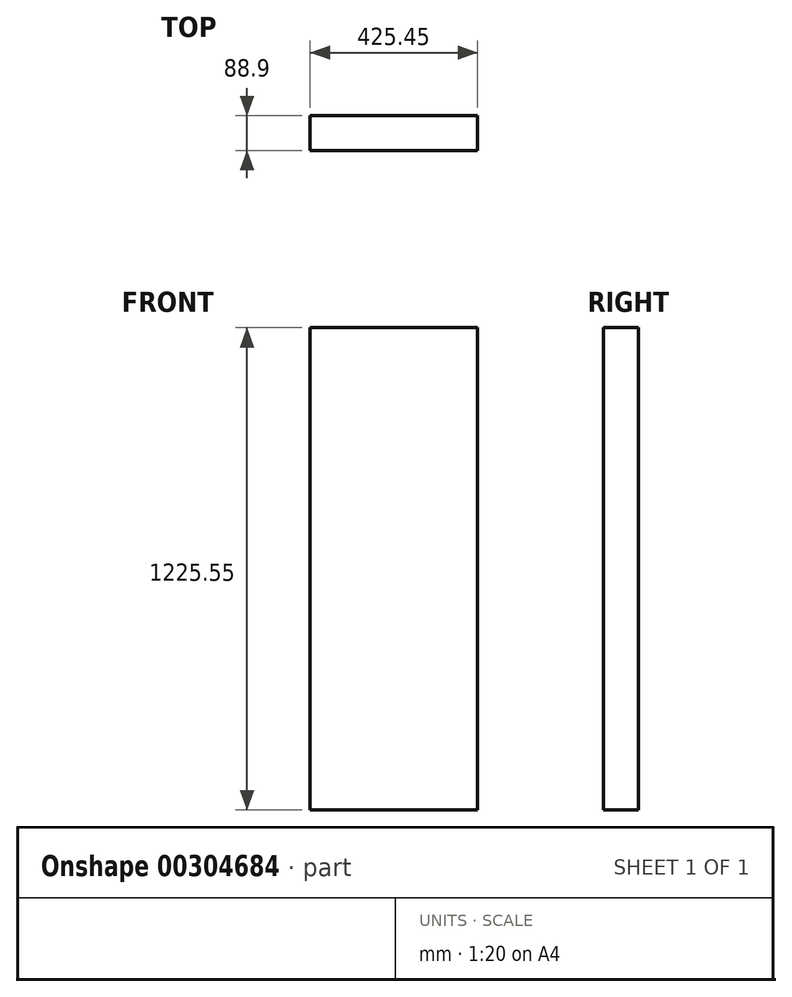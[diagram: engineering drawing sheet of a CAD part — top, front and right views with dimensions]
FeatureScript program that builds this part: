
annotation { "Feature Type Name" : "Feature", "Feature Type Description" : "" }
export const myFeature = defineFeature(function(context is Context, id is Id, definition is map)
    precondition{}
    {
        {
            var Q0;
            Q0=qCreatedBy(makeId("Front.planeOp"),FACE);
            var sketch = newSketch(context, id + "F0", { "sketchPlane" : qUnion([Q0])});
            skLineSegment(sketch, "E0.bottom", {"start": v(-210.24, 824.34) * mm, "end": v(215.21, 824.34) * mm});
            skLineSegment(sketch, "E0.top", {"start": v(-210.24, -401.21) * mm, "end": v(215.21, -401.21) * mm});
            skLineSegment(sketch, "E0.left", {"start": v(-210.24, 824.34) * mm, "end": v(-210.24, -401.21) * mm});
            skLineSegment(sketch, "E0.right", {"start": v(215.21, 824.34) * mm, "end": v(215.21, -401.21) * mm});
            skSolve(sketch);
        }
        {
            var Q0;
            Q0=makeQuery(id+"F0.imprint","IMPRINT",FACE,{"disambiguationData":[TD([[makeQuery(id+"F0.imprint","IMPRINT",EDGE,{"derivedFrom":sQuery(id+"F0.wireOp",EDGE,"E0.bottom")}),-1.0]])]});
            extrude(context, id + "F1", {"entities" : qUnion([Q0]), "depth" : 88.9 * mm});
        }
    });
